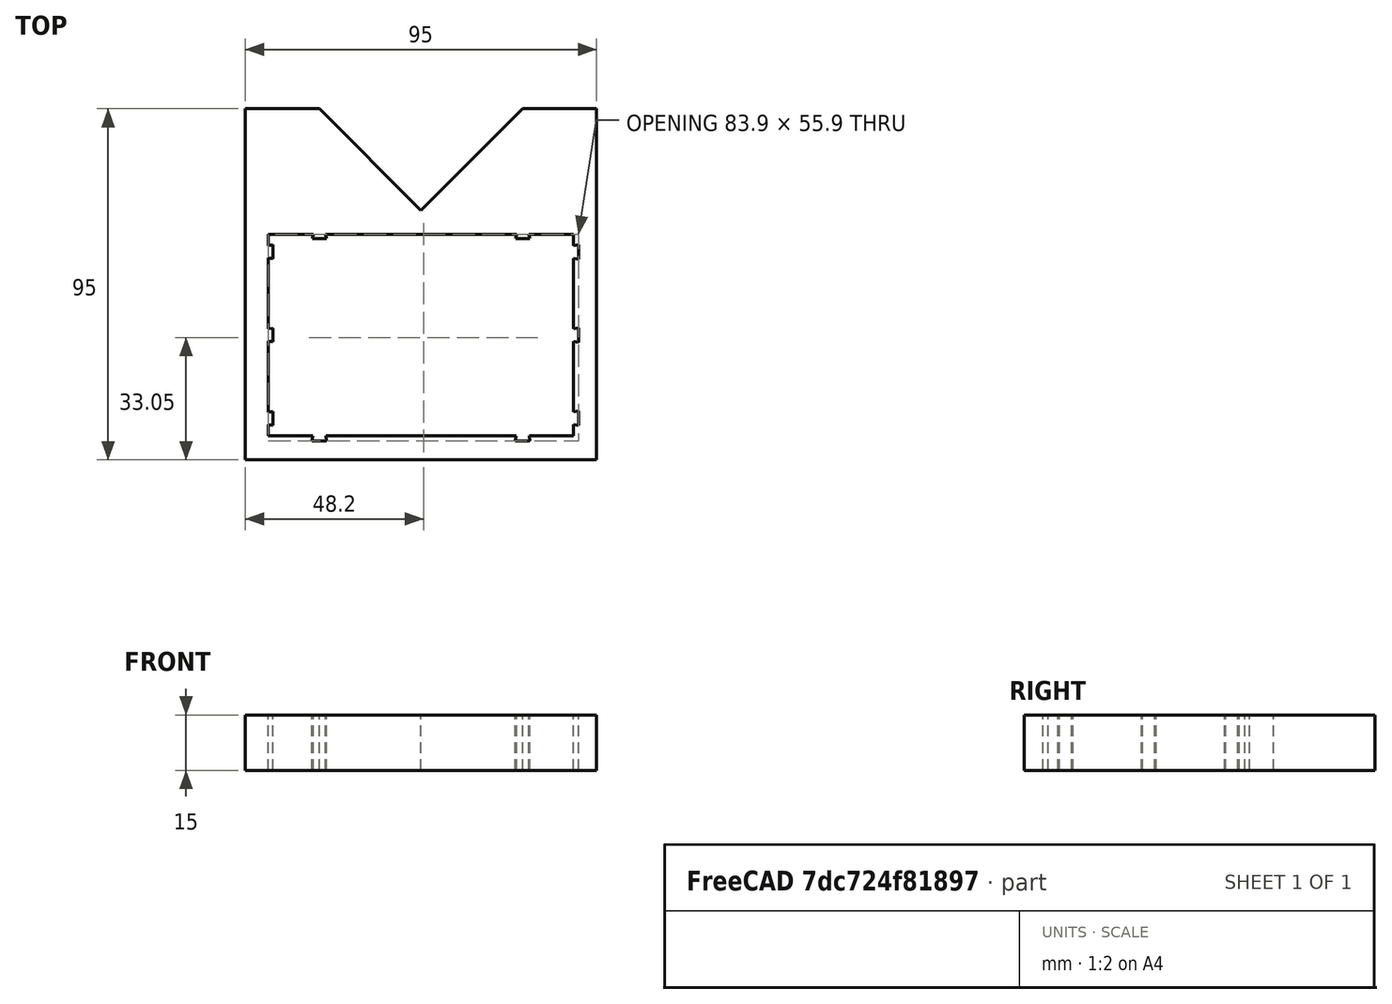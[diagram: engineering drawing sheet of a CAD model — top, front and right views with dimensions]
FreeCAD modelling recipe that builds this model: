
FCSTD DOCUMENT  (FreeCAD 0.18R15969 (Git))
Label: eternal_magnet_alignment_jig_1
License: All rights reserved
LicenseURL: http://en.wikipedia.org/wiki/All_rights_reserved
objects: Sketcher::SketchObject×1, PartDesign::Pad×1, PartDesign::Body×1
note: 4 computed .brp shape members not serialized (recipe doc carries the construction recipe); baked Part::Feature solids carry a one-line shape summary decoded from their .brp

FEATURE [Sketcher::SketchObject] Sketch
  MapMode = 5
  Support = -> [XY_Plane]
  sketch-geometry (97):
    g0: LineSegment StartX=0 StartY=67.5 StartZ=0 EndX=-27.5 EndY=95 EndZ=0
    g1: LineSegment StartX=-27.5 StartY=95 StartZ=0 EndX=-47.5 EndY=95 EndZ=0
    g2: LineSegment StartX=-47.5 StartY=95 StartZ=0 EndX=-47.5 EndY=0 EndZ=0
    g3: LineSegment StartX=47.5 StartY=0 StartZ=0 EndX=47.5 EndY=95 EndZ=0
    g4: LineSegment StartX=47.5 StartY=95 StartZ=0 EndX=27.5 EndY=95 EndZ=0
    g5: LineSegment StartX=27.5 StartY=95 StartZ=0 EndX=0 EndY=67.5 EndZ=0
    g6: LineSegment [constr] StartX=-27.5 StartY=95 StartZ=0 EndX=0 EndY=95 EndZ=0
    g7: LineSegment [constr] StartX=0 StartY=95 StartZ=0 EndX=27.5 EndY=95 EndZ=0
    g8: LineSegment [constr] StartX=0 StartY=95 StartZ=0 EndX=0 EndY=67.5 EndZ=0
    g9: LineSegment [constr] StartX=-41.25 StartY=6.5 StartZ=0 EndX=41.25 EndY=6.5 EndZ=0
    g10: LineSegment [constr] StartX=41.25 StartY=6.5 StartZ=0 EndX=41.25 EndY=61 EndZ=0
    g11: LineSegment [constr] StartX=41.25 StartY=61 StartZ=0 EndX=-41.25 EndY=61 EndZ=0
    g12: LineSegment [constr] StartX=-41.25 StartY=61 StartZ=0 EndX=-41.25 EndY=6.5 EndZ=0
    g13: LineSegment [constr] StartX=-41.25 StartY=61 StartZ=0 EndX=0 EndY=33.75 EndZ=0
    g14: LineSegment [constr] StartX=0 StartY=33.75 StartZ=0 EndX=41.25 EndY=61 EndZ=0
    g15: LineSegment [constr] StartX=0 StartY=33.75 StartZ=0 EndX=-41.25 EndY=6.5 EndZ=0
    g16: LineSegment StartX=-47.5 StartY=0 StartZ=0 EndX=47.5 EndY=0 EndZ=0
    g17: LineSegment [constr] StartX=0 StartY=67.5 StartZ=0 EndX=41.25 EndY=61 EndZ=0
    g18: LineSegment [constr] StartX=41.25 StartY=6.5 StartZ=0 EndX=0 EndY=0 EndZ=0
    g19: LineSegment StartX=-41.25 StartY=61 StartZ=0 EndX=-29.15 EndY=61 EndZ=0
    g20: LineSegment StartX=-29.15 StartY=61 StartZ=0 EndX=-29.4 EndY=59.8 EndZ=0
    g21: LineSegment StartX=-29.4 StartY=59.8 StartZ=0 EndX=-25.6 EndY=59.8 EndZ=0
    g22: LineSegment StartX=-25.6 StartY=59.8 StartZ=0 EndX=-25.85 EndY=61 EndZ=0
    g23: LineSegment StartX=-25.85 StartY=61 StartZ=0 EndX=25.85 EndY=61 EndZ=0
    g24: LineSegment StartX=25.85 StartY=61 StartZ=0 EndX=25.6 EndY=59.8 EndZ=0
    g25: LineSegment StartX=25.6 StartY=59.8 StartZ=0 EndX=29.4 EndY=59.8 EndZ=0
    g26: LineSegment StartX=29.4 StartY=59.8 StartZ=0 EndX=29.15 EndY=61 EndZ=0
    g27: LineSegment StartX=29.15 StartY=61 StartZ=0 EndX=41.25 EndY=61 EndZ=0
    g28: LineSegment StartX=-41.25 StartY=61 StartZ=0 EndX=-41.25 EndY=57.9 EndZ=0
    g29: LineSegment StartX=-41.25 StartY=57.9 StartZ=0 EndX=-40.05 EndY=58.15 EndZ=0
    g30: LineSegment StartX=-40.05 StartY=58.15 StartZ=0 EndX=-40.05 EndY=54.35 EndZ=0
    g31: LineSegment StartX=-40.05 StartY=54.35 StartZ=0 EndX=-41.25 EndY=54.6 EndZ=0
    g32: LineSegment StartX=-41.25 StartY=54.6 StartZ=0 EndX=-41.25 EndY=35.4 EndZ=0
    g33: LineSegment StartX=-41.25 StartY=35.4 StartZ=0 EndX=-40.05 EndY=35.65 EndZ=0
    g34: LineSegment StartX=-40.05 StartY=35.65 StartZ=0 EndX=-40.05 EndY=31.85 EndZ=0
    g35: LineSegment StartX=-40.05 StartY=31.85 StartZ=0 EndX=-41.25 EndY=32.1 EndZ=0
    g36: LineSegment [constr] StartX=-40.05 StartY=31.85 StartZ=0 EndX=-41.25 EndY=35.4 EndZ=0
    g37: LineSegment [constr] StartX=-40.05 StartY=54.35 StartZ=0 EndX=-41.25 EndY=57.9 EndZ=0
    g38: LineSegment [constr] StartX=-29.4 StartY=59.8 StartZ=0 EndX=-25.85 EndY=61 EndZ=0
    g39: LineSegment [constr] StartX=25.6 StartY=59.8 StartZ=0 EndX=29.15 EndY=61 EndZ=0
    g40: LineSegment StartX=-41.25 StartY=32.1 StartZ=0 EndX=-41.25 EndY=12.9 EndZ=0
    g41: LineSegment StartX=-41.25 StartY=12.9 StartZ=0 EndX=-40.05 EndY=13.15 EndZ=0
    g42: LineSegment StartX=-40.05 StartY=13.15 StartZ=0 EndX=-40.05 EndY=9.35 EndZ=0
    g43: LineSegment StartX=-40.05 StartY=9.35 StartZ=0 EndX=-41.25 EndY=9.6 EndZ=0
    g44: LineSegment StartX=-41.25 StartY=9.6 StartZ=0 EndX=-41.25 EndY=6.5 EndZ=0
    g45: LineSegment [constr] StartX=-41.25 StartY=12.9 StartZ=0 EndX=-40.05 EndY=9.35 EndZ=0
    g46: LineSegment [constr] StartX=0 StartY=33.75 StartZ=0 EndX=-40.05 EndY=35.65 EndZ=0
    g47: LineSegment [constr] StartX=0 StartY=33.75 StartZ=0 EndX=-40.05 EndY=31.85 EndZ=0
    g48: LineSegment [constr] StartX=-40.05 StartY=54.35 StartZ=0 EndX=0 EndY=56.25 EndZ=0
    g49: LineSegment [constr] StartX=0 StartY=56.25 StartZ=0 EndX=-40.05 EndY=58.15 EndZ=0
    g50: LineSegment [constr] StartX=-40.05 StartY=13.15 StartZ=0 EndX=0 EndY=11.25 EndZ=0
    g51: LineSegment [constr] StartX=-40.05 StartY=9.35 StartZ=0 EndX=0 EndY=11.25 EndZ=0
    g52: LineSegment [constr] StartX=0 StartY=11.25 StartZ=0 EndX=0 EndY=33.75 EndZ=0
    g53: LineSegment [constr] StartX=0 StartY=33.75 StartZ=0 EndX=0 EndY=56.25 EndZ=0
    g54: LineSegment [constr] StartX=-29.4 StartY=59.8 StartZ=0 EndX=-27.5 EndY=6.5 EndZ=0
    g55: LineSegment [constr] StartX=-27.5 StartY=6.5 StartZ=0 EndX=-25.6 EndY=59.8 EndZ=0
    g56: LineSegment [constr] StartX=29.4 StartY=59.8 StartZ=0 EndX=27.5 EndY=6.5 EndZ=0
    g57: LineSegment [constr] StartX=25.6 StartY=59.8 StartZ=0 EndX=27.5 EndY=6.5 EndZ=0
    g58: LineSegment [constr] StartX=-27.5 StartY=6.5 StartZ=0 EndX=0 EndY=33.75 EndZ=0
    g59: LineSegment [constr] StartX=0 StartY=33.75 StartZ=0 EndX=27.5 EndY=6.5 EndZ=0
    g60: LineSegment StartX=41.25 StartY=61 StartZ=0 EndX=41.25 EndY=58 EndZ=0
    g61: LineSegment StartX=41.25 StartY=58 StartZ=0 EndX=42.65 EndY=58.25 EndZ=0
    g62: LineSegment StartX=42.65 StartY=58.25 StartZ=0 EndX=42.65 EndY=54.25 EndZ=0
    g63: LineSegment StartX=42.65 StartY=54.25 StartZ=0 EndX=41.25 EndY=54.5 EndZ=0
    g64: LineSegment StartX=41.25 StartY=54.5 StartZ=0 EndX=41.25 EndY=35.5 EndZ=0
    g65: LineSegment StartX=41.25 StartY=35.5 StartZ=0 EndX=42.65 EndY=35.75 EndZ=0
    g66: LineSegment StartX=42.65 StartY=35.75 StartZ=0 EndX=42.65 EndY=31.75 EndZ=0
    g67: LineSegment StartX=42.65 StartY=31.75 StartZ=0 EndX=41.25 EndY=32 EndZ=0
    g68: LineSegment StartX=41.25 StartY=32 StartZ=0 EndX=41.25 EndY=13 EndZ=0
    g69: LineSegment StartX=41.25 StartY=13 StartZ=0 EndX=42.65 EndY=13.25 EndZ=0
    g70: LineSegment StartX=42.65 StartY=13.25 StartZ=0 EndX=42.65 EndY=9.25 EndZ=0
    g71: LineSegment StartX=42.65 StartY=9.25 StartZ=0 EndX=41.25 EndY=9.5 EndZ=0
    g72: LineSegment StartX=41.25 StartY=9.5 StartZ=0 EndX=41.25 EndY=6.5 EndZ=0
    g73: LineSegment StartX=-41.25 StartY=6.5 StartZ=0 EndX=-29.25 EndY=6.5 EndZ=0
    g74: LineSegment StartX=-29.25 StartY=6.5 StartZ=0 EndX=-29.5 EndY=5.1 EndZ=0
    g75: LineSegment StartX=-29.5 StartY=5.1 StartZ=0 EndX=-25.5 EndY=5.1 EndZ=0
    g76: LineSegment StartX=-25.5 StartY=5.1 StartZ=0 EndX=-25.75 EndY=6.5 EndZ=0
    g77: LineSegment StartX=-25.75 StartY=6.5 StartZ=0 EndX=25.75 EndY=6.5 EndZ=0
    g78: LineSegment StartX=25.75 StartY=6.5 StartZ=0 EndX=25.5 EndY=5.1 EndZ=0
    g79: LineSegment StartX=25.5 StartY=5.1 StartZ=0 EndX=29.5 EndY=5.1 EndZ=0
    g80: LineSegment StartX=29.5 StartY=5.1 StartZ=0 EndX=29.25 EndY=6.5 EndZ=0
    g81: LineSegment StartX=29.25 StartY=6.5 StartZ=0 EndX=41.25 EndY=6.5 EndZ=0
    g82: LineSegment [constr] StartX=-29.5 StartY=5.1 StartZ=0 EndX=-27.5 EndY=6.5 EndZ=0
    g83: LineSegment [constr] StartX=-27.5 StartY=6.5 StartZ=0 EndX=-25.5 EndY=5.1 EndZ=0
    g84: LineSegment [constr] StartX=25.5 StartY=5.1 StartZ=0 EndX=27.5 EndY=6.5 EndZ=0
    g85: LineSegment [constr] StartX=27.5 StartY=6.5 StartZ=0 EndX=29.5 EndY=5.1 EndZ=0
    g86: LineSegment [constr] StartX=42.65 StartY=13.25 StartZ=0 EndX=0 EndY=11.25 EndZ=0
    g87: LineSegment [constr] StartX=0 StartY=11.25 StartZ=0 EndX=42.65 EndY=9.25 EndZ=0
    g88: LineSegment [constr] StartX=42.65 StartY=31.75 StartZ=0 EndX=0 EndY=33.75 EndZ=0
    g89: LineSegment [constr] StartX=0 StartY=33.75 StartZ=0 EndX=42.65 EndY=35.75 EndZ=0
    g90: LineSegment [constr] StartX=42.65 StartY=54.25 StartZ=0 EndX=0 EndY=56.25 EndZ=0
    g91: LineSegment [constr] StartX=0 StartY=56.25 StartZ=0 EndX=42.65 EndY=58.25 EndZ=0
    g92: LineSegment [constr] StartX=-29.25 StartY=6.5 StartZ=0 EndX=-25.5 EndY=5.1 EndZ=0
    g93: LineSegment [constr] StartX=25.75 StartY=6.5 StartZ=0 EndX=29.5 EndY=5.1 EndZ=0
    g94: LineSegment [constr] StartX=41.25 StartY=9.5 StartZ=0 EndX=42.65 EndY=13.25 EndZ=0
    g95: LineSegment [constr] StartX=41.25 StartY=32 StartZ=0 EndX=42.65 EndY=35.75 EndZ=0
    g96: LineSegment [constr] StartX=41.25 StartY=54.5 StartZ=0 EndX=42.65 EndY=58.25 EndZ=0
  constraints (259):
    c: PointOnObject(g0,g-2)
    c: Coincident(g0,g1)
    c: Coincident(g1,g2)
    c: PointOnObject(g2,g-1)
    c: Vertical(g2)
    c: PointOnObject(g3,g-1)
    c: Vertical(g3)
    c: Coincident(g3,g4)
    c: Coincident(g4,g5)
    c: Coincident(g5,g0)
    c: Coincident(g6,g0)
    c: PointOnObject(g6,g-2)
    c: Coincident(g7,g6)
    c: Coincident(g7,g4)
    c: Horizontal(g7)
    c: Horizontal(g6)
    c: Coincident(g8,g6)
    c: Coincident(g8,g0)
    c: Equal(g8,g6)
    c: Equal(g6,g7)
    c: Horizontal(g1)
    c: Horizontal(g4)
    c: Equal(g4,g1)
    c: DistanceX(g1,g1) = 20
    c: Coincident(g9,g10)
    c: Coincident(g10,g11)
    c: Coincident(g11,g12)
    c: Coincident(g12,g9)
    c: Horizontal(g9)
    c: Horizontal(g11)
    c: Vertical(g10)
    c: Vertical(g12)
    c: DistanceX(g11,g11) = 82.5
    c: DistanceY(g10,g10) = 54.5
    c: Coincident(g13,g11)
    c: PointOnObject(g13,g-2)
    c: Coincident(g14,g13)
    c: Coincident(g14,g10)
    c: Coincident(g15,g13)
    c: Coincident(g15,g9)
    c: Equal(g15,g13)
    c: Equal(g13,g14)
    c: Coincident(g16,g2)
    c: Coincident(g16,g3)
    c: DistanceX(g16,g16) = 95
    c: DistanceY(g2,g2) = 95
    c: Coincident(g17,g0)
    c: Coincident(g17,g10)
    c: Coincident(g18,g9)
    c: Coincident(g18,g-1)
    c: Equal(g18,g17)
    c: Coincident(g11,g19)
    c: Coincident(g19,g20)
    c: Coincident(g20,g21)
    c: Horizontal(g21)
    c: Coincident(g21,g22)
    c: Coincident(g22,g23)
    c: Coincident(g23,g24)
    c: Coincident(g24,g25)
    c: Horizontal(g25)
    c: Coincident(g25,g26)
    c: Coincident(g26,g27)
    c: Coincident(g27,g10)
    c: PointOnObject(g26,g11)
    c: PointOnObject(g23,g11)
    c: PointOnObject(g22,g11)
    c: PointOnObject(g19,g11)
    c: Equal(g20,g22)
    c: Equal(g24,g26)
    c: Coincident(g19,g28)
    c: Coincident(g28,g29)
    c: Coincident(g29,g30)
    c: Vertical(g30)
    c: Coincident(g30,g31)
    c: Coincident(g31,g32)
    c: Coincident(g32,g33)
    c: Coincident(g33,g34)
    c: Vertical(g34)
    c: Coincident(g34,g35)
    c: PointOnObject(g35,g12)
    c: PointOnObject(g32,g12)
    c: PointOnObject(g31,g12)
    c: PointOnObject(g28,g12)
    c: Equal(g20,g29)
    c: Equal(g29,g31)
    c: Equal(g31,g33)
    c: Equal(g33,g35)
    c: Equal(g34,g30)
    c: Equal(g30,g21)
    c: Equal(g21,g25)
    c: Coincident(g36,g34)
    c: Coincident(g36,g32)
    c: Coincident(g37,g30)
    c: Coincident(g37,g28)
    c: Coincident(g38,g20)
    c: Coincident(g38,g22)
    c: Coincident(g39,g24)
    c: Coincident(g39,g26)
    c: Equal(g38,g39)
    c: Equal(g39,g37)
    c: Equal(g37,g36)
    c: Coincident(g35,g40)
    c: Coincident(g40,g41)
    c: Coincident(g41,g42)
    c: Vertical(g42)
    c: Coincident(g42,g43)
    c: Coincident(g43,g44)
    c: Coincident(g44,g9)
    c: PointOnObject(g43,g12)
    c: PointOnObject(g40,g12)
    c: Equal(g42,g34)
    c: Equal(g41,g43)
    c: Equal(g43,g35)
    c: Coincident(g45,g40)
    c: Coincident(g45,g42)
    c: Equal(g45,g36)
    c: Coincident(g46,g13)
    c: Coincident(g46,g33)
    c: Coincident(g47,g13)
    c: Coincident(g47,g34)
    c: Coincident(g48,g30)
    c: PointOnObject(g48,g-2)
    c: Coincident(g49,g48)
    c: Coincident(g49,g29)
    c: Coincident(g50,g41)
    c: PointOnObject(g50,g-2)
    c: Coincident(g51,g42)
    c: Coincident(g51,g50)
    c: Coincident(g52,g50)
    c: Coincident(g52,g13)
    c: Coincident(g53,g13)
    c: Coincident(g53,g48)
    c: Equal(g53,g52)
    c: DistanceY(g50,g48) = 45
    c: DistanceY(g31,g28) = 3.3
    c: DistanceY(g30,g30) = 3.8
    c: DistanceX(g31,g31) = 1.2
    c: Coincident(g54,g20)
    c: PointOnObject(g54,g9)
    c: Coincident(g55,g54)
    c: Coincident(g55,g21)
    c: Coincident(g56,g25)
    c: PointOnObject(g56,g9)
    c: Coincident(g57,g24)
    c: Coincident(g57,g56)
    c: Equal(g56,g57)
    c: Equal(g57,g54)
    c: Equal(g54,g55)
    c: Coincident(g58,g54)
    c: Coincident(g58,g13)
    c: Coincident(g59,g13)
    c: Coincident(g59,g56)
    c: Equal(g58,g59)
    c: DistanceX(g54,g56) = 55
    c: Coincident(g27,g60)
    c: Coincident(g60,g61)
    c: Coincident(g61,g62)
    c: Vertical(g62)
    c: Coincident(g62,g63)
    c: Coincident(g63,g64)
    c: Coincident(g64,g65)
    c: Coincident(g65,g66)
    c: Vertical(g66)
    c: Coincident(g66,g67)
    c: Coincident(g67,g68)
    c: Coincident(g68,g69)
    c: Coincident(g69,g70)
    c: Vertical(g70)
    c: Coincident(g70,g71)
    c: Coincident(g71,g72)
    c: Coincident(g72,g9)
    c: PointOnObject(g68,g10)
    c: PointOnObject(g71,g10)
    c: PointOnObject(g67,g10)
    c: PointOnObject(g64,g10)
    c: PointOnObject(g63,g10)
    c: PointOnObject(g60,g10)
    c: Coincident(g44,g73)
    c: Coincident(g73,g74)
    c: Coincident(g74,g75)
    c: Horizontal(g75)
    c: Coincident(g75,g76)
    c: Coincident(g77,g78)
    c: Coincident(g78,g79)
    c: Horizontal(g79)
    c: Coincident(g79,g80)
    c: Coincident(g80,g81)
    c: Coincident(g81,g72)
    c: PointOnObject(g73,g9)
    c: PointOnObject(g76,g9)
    c: PointOnObject(g77,g9)
    c: PointOnObject(g80,g9)
    c: Equal(g79,g70)
    c: Equal(g70,g66)
    c: Equal(g66,g62)
    c: Equal(g76,g74)
    c: Equal(g78,g80)
    c: Equal(g80,g71)
    c: Equal(g71,g69)
    c: Equal(g69,g67)
    c: Equal(g67,g65)
    c: Equal(g65,g63)
    c: Equal(g63,g61)
    c: Coincident(g82,g74)
    c: Coincident(g82,g54)
    c: Coincident(g83,g54)
    c: Coincident(g83,g75)
    c: Coincident(g77,g76)
    c: Coincident(g84,g78)
    c: Coincident(g84,g56)
    c: Coincident(g85,g56)
    c: Coincident(g85,g79)
    c: Coincident(g86,g69)
    c: Coincident(g86,g50)
    c: Coincident(g87,g50)
    c: Coincident(g87,g70)
    c: Coincident(g88,g66)
    c: Coincident(g88,g13)
    c: Coincident(g89,g13)
    c: Coincident(g89,g65)
    c: Coincident(g90,g62)
    c: Coincident(g90,g48)
    c: Coincident(g91,g48)
    c: Coincident(g91,g61)
    c: Equal(g87,g86)
    c: Equal(g88,g89)
    c: Equal(g90,g91)
    c: Equal(g82,g83)
    c: Equal(g84,g85)
    c: Equal(g75,g79)
    c: DistanceY(g74,g73) = 1.4
    c: Equal(g74,g76)
    c: Equal(g76,g78)
    c: Equal(g78,g80)
    c: Equal(g80,g71)
    c: Equal(g71,g69)
    c: Equal(g69,g67)
    c: Equal(g67,g65)
    c: Equal(g65,g63)
    c: Equal(g63,g61)
    c: Coincident(g92,g73)
    c: Coincident(g92,g75)
    c: Coincident(g93,g77)
    c: Coincident(g93,g79)
    c: Coincident(g94,g71)
    c: Coincident(g94,g69)
    c: Coincident(g95,g67)
    c: Coincident(g95,g65)
    c: Coincident(g96,g63)
    c: Coincident(g96,g61)
    c: Equal(g96,g95)
    c: Equal(g95,g94)
    c: Equal(g94,g93)
    c: Equal(g93,g92)
    c: DistanceX(g75,g75) = 4
    c: DistanceX(g73,g76) = 3.5
    c: Equal(g47,g46)
    c: Equal(g49,g48)
    c: Equal(g51,g50)
FEATURE [PartDesign::Pad] Pad
  Length = 15
  Length2 = 100
  Profile = -> Sketch
  Refine = true
  Type = 0
FEATURE [PartDesign::Body] Body
  Group = -> [Sketch,Pad]
  Origin = -> Origin
  Tip = -> Pad
